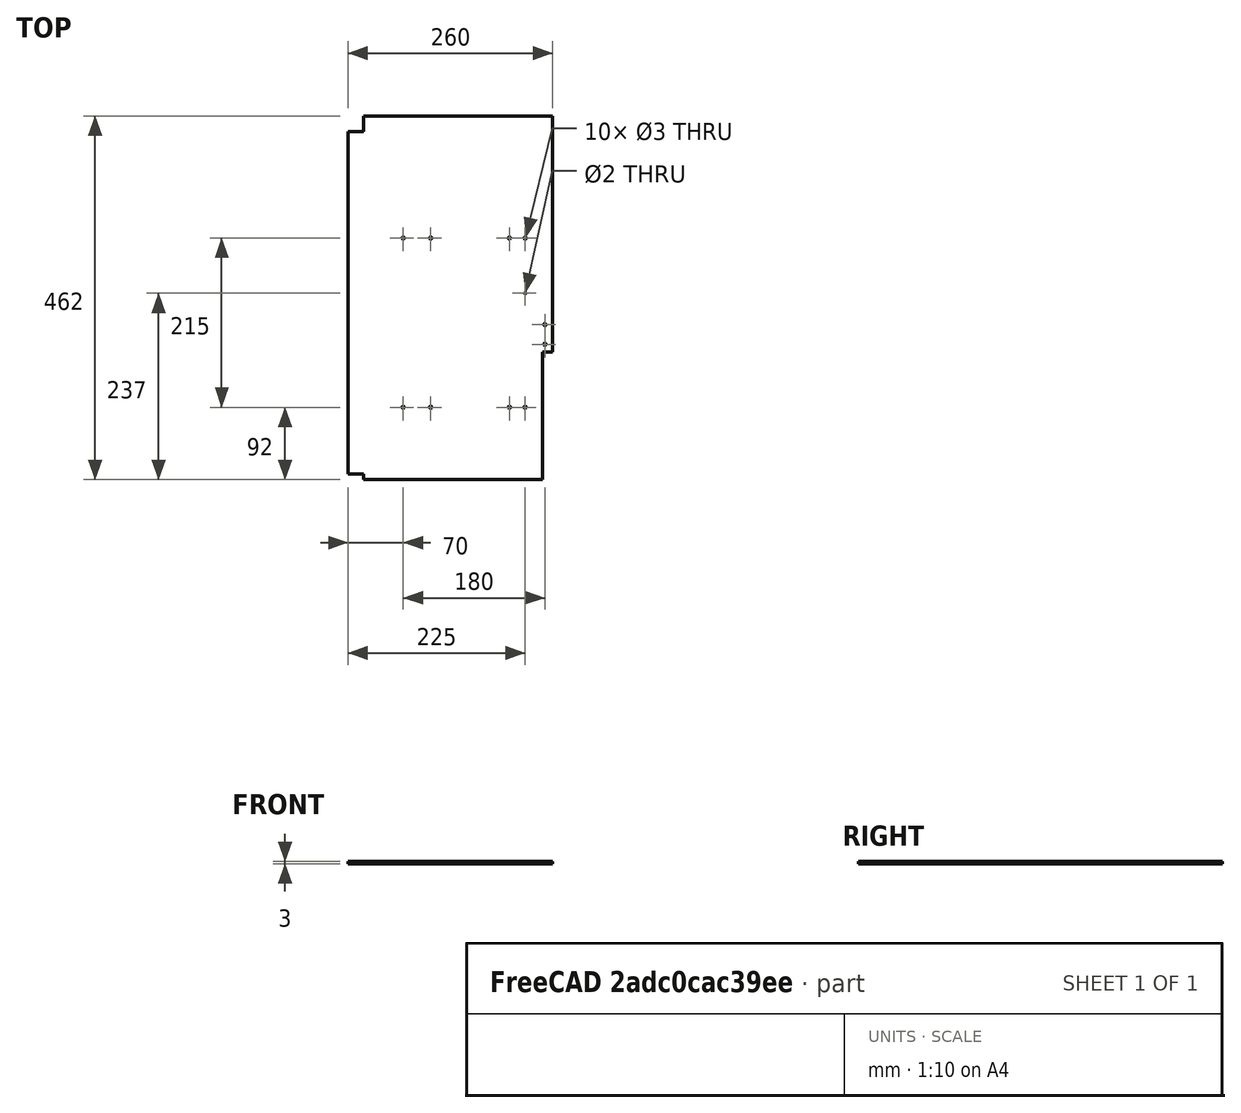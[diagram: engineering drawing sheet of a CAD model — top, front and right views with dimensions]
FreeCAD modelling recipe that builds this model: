
FCSTD DOCUMENT  (FreeCAD 0.18R)
Label: K-MINI-Enclosure-BottomChamberSheet
License: All rights reserved
LicenseURL: http://en.wikipedia.org/wiki/All_rights_reserved
objects: Drawing::FeatureViewPython×19, Sketcher::SketchObject×1, PartDesign::Pad×1, PartDesign::Body×1, App::Part×1, Drawing::FeatureViewPart×1, Drawing::FeaturePage×1
note: 4 computed .brp shape members not serialized (recipe doc carries the construction recipe); baked Part::Feature solids carry a one-line shape summary decoded from their .brp

FEATURE [Sketcher::SketchObject] Sketch020
  MapMode = 5
  Support = -> [XY_Plane042]
  sketch-geometry (21):
    g0: LineSegment StartX=-205 StartY=-237 StartZ=0 EndX=22 EndY=-237 EndZ=0
    g1: LineSegment StartX=35 StartY=225 StartZ=0 EndX=-205 EndY=225 EndZ=0
    g2: LineSegment StartX=-205 StartY=225 StartZ=0 EndX=-205 EndY=205 EndZ=0
    g3: LineSegment StartX=-205 StartY=205 StartZ=0 EndX=-225 EndY=205 EndZ=0
    g4: LineSegment StartX=-225 StartY=205 StartZ=0 EndX=-225 EndY=-230 EndZ=0
    g5: LineSegment StartX=-225 StartY=-230 StartZ=0 EndX=-205 EndY=-230 EndZ=0
    g6: LineSegment StartX=-205 StartY=-230 StartZ=0 EndX=-205 EndY=-237 EndZ=0
    g7: Circle CenterX=-155 CenterY=70 CenterZ=0 NormalX=0 NormalY=0 NormalZ=1 AngleXU=0 Radius=1.5
    g8: Circle CenterX=-120 CenterY=70 CenterZ=0 NormalX=0 NormalY=0 NormalZ=1 AngleXU=0 Radius=1.5
    g9: Circle CenterX=25 CenterY=-40 CenterZ=0 NormalX=0 NormalY=0 NormalZ=1 AngleXU=0 Radius=1.5
    g10: Circle CenterX=25 CenterY=-65 CenterZ=0 NormalX=0 NormalY=0 NormalZ=1 AngleXU=0 Radius=1.5
    g11: Circle CenterX=-120 CenterY=-145 CenterZ=0 NormalX=0 NormalY=0 NormalZ=1 AngleXU=0 Radius=1.5
    g12: Circle CenterX=-155 CenterY=-145 CenterZ=0 NormalX=0 NormalY=0 NormalZ=1 AngleXU=0 Radius=1.5
    g13: Circle CenterX=0 CenterY=0 CenterZ=0 NormalX=0 NormalY=0 NormalZ=1 AngleXU=0 Radius=1
    g14: Circle CenterX=-20 CenterY=70 CenterZ=0 NormalX=0 NormalY=0 NormalZ=1 AngleXU=0 Radius=1.5
    g15: Circle CenterX=0 CenterY=70 CenterZ=0 NormalX=0 NormalY=0 NormalZ=1 AngleXU=0 Radius=1.5
    g16: Circle CenterX=-20 CenterY=-145 CenterZ=0 NormalX=0 NormalY=0 NormalZ=1 AngleXU=0 Radius=1.5
    g17: Circle CenterX=0 CenterY=-145 CenterZ=0 NormalX=0 NormalY=0 NormalZ=1 AngleXU=0 Radius=1.5
    g18: LineSegment StartX=22 StartY=-237 StartZ=0 EndX=22 EndY=-75 EndZ=0
    g19: LineSegment StartX=22 StartY=-75 StartZ=0 EndX=35 EndY=-75 EndZ=0
    g20: LineSegment StartX=35 StartY=-75 StartZ=0 EndX=35 EndY=225 EndZ=0
  constraints (62):
    c: Coincident(g1,g2)
    c: Coincident(g2,g3)
    c: Coincident(g3,g4)
    c: Coincident(g4,g5)
    c: Coincident(g5,g6)
    c: Horizontal(g0)
    c: Horizontal(g1)
    c: Horizontal(g5)
    c: Vertical(g4)
    c: Vertical(g2)
    c: Vertical(g6)
    c: Horizontal(g3)
    c: DistanceY(g2,g2) = 20
    c: DistanceX(g3,g3) = 20
    c: DistanceX(g5,g5) = 20
    c: DistanceY(g6,g6) = 7
    c: DistanceX(g1,g-1) = 205
    c: DistanceY(g-1,g1) = 225
    c: Coincident(g0,g6)
    c: Radius(g12) = 1.5
    c: Equal(g10,g9)
    c: Equal(g9,g8)
    c: Equal(g8,g7)
    c: Equal(g7,g11)
    c: Equal(g11,g12)
    c: Horizontal(g7,g8)
    c: Vertical(g9,g10)
    c: Horizontal(g11,g12)
    c: DistanceY(g-1,g7) = 70
    c: DistanceY(g12,g-1) = 145
    c: DistanceX(g7,g8) = 35
    c: DistanceY(g10,g9) = 25
    c: DistanceY(g9,g-1) = 40
    c: DistanceX(g-1,g9) = 25
    c: Coincident(g13,g-1)
    c: Radius(g13) = 1
    c: Horizontal(g14,g15)
    c: Horizontal(g15,g8)
    c: Horizontal(g11,g16)
    c: Horizontal(g16,g17)
    c: DistanceX(g8,g15) = 120
    c: DistanceX(g14,g15) = 20
    c: Vertical(g15,g17)
    c: Vertical(g14,g16)
    c: Equal(g8,g14)
    c: Equal(g14,g15)
    c: Equal(g15,g16)
    c: Equal(g16,g17)
    c: DistanceY(g0,g13) = 237
    c: Coincident(g19,g20)
    c: Coincident(g0,g18)
    c: Coincident(g18,g19)
    c: Horizontal(g19)
    c: Vertical(g20)
    c: Vertical(g18)
    c: DistanceX(g13,g0) = 22
    c: Vertical(g11,g8)
    c: Vertical(g12,g7)
    c: DistanceY(g18,g18) = 162
    c: PointOnObject(g17,g-2)
    c: DistanceX(g3,g20) = 260
    c: Coincident(g1,g20)
FEATURE [PartDesign::Pad] Pad034
  Length = 3
  Length2 = 100
  Profile = -> Sketch020
  Type = 0
FEATURE [PartDesign::Body] Body035  label="BottomEnclosureSheet"
  Group = -> [Sketch020,Pad034]
  Origin = -> Origin042
  Placement = pos=(0,0,-30) rot=(0,0,1;0rad)
  Tip = -> Pad034
FEATURE [App::Part] Part002  label="K-MINI-Enclosure-BottomChamberSheet"
  Group = -> [Body035]
  Origin = -> Origin004
FEATURE [Drawing::FeatureViewPart] View
  Direction = (0,0,1)
  HiddenWidth = 0.15
  LineWidth = 0.35
  Rotation = 90
  ShowHiddenLines = false
  ShowSmoothLines = false
  Source = -> Body035
  Tolerance = 0.05
  ViewResult = <g id="View"\n   transform="rotate(90,300,300) translate(300,300) scale(1,1)"\n  >\n<g   fill="none"\n   stroke="rgb(0, 0, 0)"\n   stroke-linecap="butt"\n   stroke-linejoin="miter"\n   stroke-width="0.350000"\n   transform="scale(1,-1)"\n  >\n<path id= "1" d=" M -205 -237 L 22 -237 " />\n<path id= "2" d=" M 22 -237 L 22 -75 " />\n<path id= "3" d=" M 22 -75 L 35 -75 " />\n<path id= "4" d=" M 35 -75 L 35 225 " />\n<path id= "5" d=" M 35 225 L -205 225 " />\n<path id= "6" d=" M -205 225 L -205 205 " />\n<path id= "7" d=" M -205 205 L -225 205 " />\n<path id= "8" d=" M -225 205 L -225 -230 " />\n<path id= "9" d=" M -225 -230 L -205 -230 " />\n<path id= "10" d=" M -205 -230 L -205 -237 " />\n<circle cx ="0" cy ="-145" r ="1.5" /><circle cx ="-20" cy ="-145" r ="1.5" /><circle cx ="0" cy ="70" r ="1.5" /><circle cx ="-20" cy ="70" r ="1.5" /><circle cx ="-155" cy ="-145" r ="1.5" /><circle cx ="-120" cy ="-145" r ="1.5" /><circle cx ="25" cy ="-65" r ="1.5" /><circle cx ="25" cy ="-40" r ="1.5" /><circle cx ="-120" cy ="70" r ="1.5" /><circle cx ="-155" cy ="70" r ="1.5" /><circle cx ="0" cy ="0" r ="1" /></g>\n</g>
  Visible = true
  X = 300
  Y = 300
FEATURE [Drawing::FeatureViewPython] dim001  # drawing view (typed FeaturePython)
  Rotation = 0
  ViewResult = <g> \n  <line x1="68.000000" y1="75.000000" x2="30.314251" y2="75.000000" style="stroke:rgb(0,0,255);stroke-width:0.50" />\n<line x1="61.000000" y1="322.000000" x2="30.314251" y2="322.000000" style="stroke:rgb(0,0,255);stroke-width:0.50" />\n<line x1="31.314251" y1="75.000000" x2="31.314251" y2="322.000000" style="stroke:rgb(0,0,255);stroke-width:0.50" /> \n  <polygon points="31.314251,322.000000 32.314251,319.000000 31.314251,318.000000 30.314251,319.000000" style="fill:rgb(0,0,255);stroke:rgb(0,0,255);stroke-width:0" /><polygon points="31.314251,75.000000 30.314251,78.000000 31.314251,79.000000 32.314251,78.000000" style="fill:rgb(0,0,255);stroke:rgb(0,0,255);stroke-width:0" /> \n  <text x="29.314251" y="198.500000" font-family="inherit" font-size="3.6" fill="rgb(0,0,255)" text-anchor="middle" transform="rotate(-90.000000 29.314251,198.500000)" >247</text> </g>
  Visible = true
  X = 0
  Y = 0
  arrowL1 = 3
  arrowL2 = 1
  arrowW = 2
  arrow_scheme = 0
  autoPlaceOffset = 2
  autoPlaceText = true
  click1_x = 31.3143
  click1_y = 315.491
  click2_x = 31.3143
  click2_y = 315.491
  comma_decimal_place = false
  dimension_line_overshoot = 1
  gap_datum_points = 2
  halfDimension_linear = false
  lineColor = rgb(0,0,255)
  strokeWidth = 0.5
  textFormat_linear = %(value)3.3f
  textRenderer_color = rgb(0,0,255)
  textRenderer_family = inherit
  textRenderer_size = 3.6
  unit_custom_scale = 1
  unit_scheme = 0
FEATURE [Drawing::FeatureViewPython] dim002  # drawing view (typed FeaturePython)
  Rotation = 0
  ViewResult = <g> \n  <line x1="68.000000" y1="75.000000" x2="45.188520" y2="75.000000" style="stroke:rgb(0,0,255);stroke-width:0.50" />\n<line x1="68.000000" y1="95.000000" x2="45.188520" y2="95.000000" style="stroke:rgb(0,0,255);stroke-width:0.50" />\n<line x1="46.188520" y1="75.000000" x2="46.188520" y2="95.000000" style="stroke:rgb(0,0,255);stroke-width:0.50" /> \n  <polygon points="46.188520,95.000000 47.188520,92.000000 46.188520,91.000000 45.188520,92.000000" style="fill:rgb(0,0,255);stroke:rgb(0,0,255);stroke-width:0" /><polygon points="46.188520,75.000000 45.188520,78.000000 46.188520,79.000000 47.188520,78.000000" style="fill:rgb(0,0,255);stroke:rgb(0,0,255);stroke-width:0" /> \n  <text x="44.188520" y="85.000000" font-family="inherit" font-size="3.6" fill="rgb(0,0,255)" text-anchor="middle" transform="rotate(-90.000000 44.188520,85.000000)" >20</text> </g>
  Visible = true
  X = 0
  Y = 0
  arrowL1 = 3
  arrowL2 = 1
  arrowW = 2
  arrow_scheme = 0
  autoPlaceOffset = 2
  autoPlaceText = true
  click1_x = 46.1885
  click1_y = 96.6827
  click2_x = 46.1885
  click2_y = 96.6827
  comma_decimal_place = false
  dimension_line_overshoot = 1
  gap_datum_points = 2
  halfDimension_linear = false
  lineColor = rgb(0,0,255)
  strokeWidth = 0.5
  textFormat_linear = %(value)3.3f
  textRenderer_color = rgb(0,0,255)
  textRenderer_family = inherit
  textRenderer_size = 3.6
  unit_custom_scale = 1
  unit_scheme = 0
FEATURE [Drawing::FeatureViewPython] dim003  # drawing view (typed FeaturePython)
  Rotation = 0
  ViewResult = <g> \n  <line x1="63.000000" y1="93.000000" x2="63.000000" y2="60.454217" style="stroke:rgb(0,0,255);stroke-width:0.50" />\n<line x1="70.000000" y1="73.000000" x2="70.000000" y2="60.454217" style="stroke:rgb(0,0,255);stroke-width:0.50" />\n<line x1="63.000000" y1="61.454217" x2="70.000000" y2="61.454217" style="stroke:rgb(0,0,255);stroke-width:0.50" /> \n  <polygon points="70.000000,61.454217 73.000000,62.454217 74.000000,61.454217 73.000000,60.454217" style="fill:rgb(0,0,255);stroke:rgb(0,0,255);stroke-width:0" /><polygon points="63.000000,61.454217 60.000000,60.454217 59.000000,61.454217 60.000000,62.454217" style="fill:rgb(0,0,255);stroke:rgb(0,0,255);stroke-width:0" /> \n  <text x="66.500000" y="59.454217" font-family="inherit" font-size="3.6" fill="rgb(0,0,255)" text-anchor="middle" transform="rotate(0.000000 66.500000,59.454217)" >7</text> </g>
  Visible = true
  X = 0
  Y = 0
  arrowL1 = 3
  arrowL2 = 1
  arrowW = 2
  arrow_scheme = 0
  autoPlaceOffset = 2
  autoPlaceText = true
  click1_x = 64.5856
  click1_y = 61.4542
  click2_x = 64.5856
  click2_y = 61.4542
  comma_decimal_place = false
  dimension_line_overshoot = 1
  gap_datum_points = 2
  halfDimension_linear = false
  lineColor = rgb(0,0,255)
  strokeWidth = 0.5
  textFormat_linear = %(value)3.3f
  textRenderer_color = rgb(0,0,255)
  textRenderer_family = inherit
  textRenderer_size = 3.6
  unit_custom_scale = 1
  unit_scheme = 0
FEATURE [Drawing::FeatureViewPython] dim004  # drawing view (typed FeaturePython)
  Rotation = 0
  ViewResult = <g> \n  <line x1="507.000000" y1="75.000000" x2="544.693676" y2="75.000000" style="stroke:rgb(0,0,255);stroke-width:0.50" />\n<line x1="507.000000" y1="95.000000" x2="544.693676" y2="95.000000" style="stroke:rgb(0,0,255);stroke-width:0.50" />\n<line x1="543.693676" y1="75.000000" x2="543.693676" y2="95.000000" style="stroke:rgb(0,0,255);stroke-width:0.50" /> \n  <polygon points="543.693676,95.000000 544.693676,92.000000 543.693676,91.000000 542.693676,92.000000" style="fill:rgb(0,0,255);stroke:rgb(0,0,255);stroke-width:0" /><polygon points="543.693676,75.000000 542.693676,78.000000 543.693676,79.000000 544.693676,78.000000" style="fill:rgb(0,0,255);stroke:rgb(0,0,255);stroke-width:0" /> \n  <text x="541.693676" y="85.000000" font-family="inherit" font-size="3.6" fill="rgb(0,0,255)" text-anchor="middle" transform="rotate(-90.000000 541.693676,85.000000)" >20</text> </g>
  Visible = true
  X = 0
  Y = 0
  arrowL1 = 3
  arrowL2 = 1
  arrowW = 2
  arrow_scheme = 0
  autoPlaceOffset = 2
  autoPlaceText = true
  click1_x = 543.694
  click1_y = 100.988
  click2_x = 543.694
  click2_y = 100.988
  comma_decimal_place = false
  dimension_line_overshoot = 1
  gap_datum_points = 2
  halfDimension_linear = false
  lineColor = rgb(0,0,255)
  strokeWidth = 0.5
  textFormat_linear = %(value)3.3f
  textRenderer_color = rgb(0,0,255)
  textRenderer_family = inherit
  textRenderer_size = 3.6
  unit_custom_scale = 1
  unit_scheme = 0
FEATURE [Drawing::FeatureViewPython] dim005  # drawing view (typed FeaturePython)
  Rotation = 0
  ViewResult = <g> \n  <line x1="527.000000" y1="95.000000" x2="544.302248" y2="95.000000" style="stroke:rgb(0,0,255);stroke-width:0.50" />\n<line x1="527.000000" y1="322.000000" x2="544.302248" y2="322.000000" style="stroke:rgb(0,0,255);stroke-width:0.50" />\n<line x1="543.302248" y1="95.000000" x2="543.302248" y2="322.000000" style="stroke:rgb(0,0,255);stroke-width:0.50" /> \n  <polygon points="543.302248,322.000000 544.302248,319.000000 543.302248,318.000000 542.302248,319.000000" style="fill:rgb(0,0,255);stroke:rgb(0,0,255);stroke-width:0" /><polygon points="543.302248,95.000000 542.302248,98.000000 543.302248,99.000000 544.302248,98.000000" style="fill:rgb(0,0,255);stroke:rgb(0,0,255);stroke-width:0" /> \n  <text x="541.302248" y="208.500000" font-family="inherit" font-size="3.6" fill="rgb(0,0,255)" text-anchor="middle" transform="rotate(-90.000000 541.302248,208.500000)" >227</text> </g>
  Visible = true
  X = 0
  Y = 0
  arrowL1 = 3
  arrowL2 = 1
  arrowW = 2
  arrow_scheme = 0
  autoPlaceOffset = 2
  autoPlaceText = true
  click1_x = 543.302
  click1_y = 328.408
  click2_x = 543.302
  click2_y = 328.408
  comma_decimal_place = false
  dimension_line_overshoot = 1
  gap_datum_points = 2
  halfDimension_linear = false
  lineColor = rgb(0,0,255)
  strokeWidth = 0.5
  textFormat_linear = %(value)3.3f
  textRenderer_color = rgb(0,0,255)
  textRenderer_family = inherit
  textRenderer_size = 3.6
  unit_custom_scale = 1
  unit_scheme = 0
FEATURE [Drawing::FeatureViewPython] dim006  # drawing view (typed FeaturePython)
  Rotation = 0
  ViewResult = <g> \n  <line x1="507.000000" y1="75.000000" x2="560.350802" y2="75.000000" style="stroke:rgb(0,0,255);stroke-width:0.50" />\n<line x1="437.000000" y1="335.000000" x2="560.350802" y2="335.000000" style="stroke:rgb(0,0,255);stroke-width:0.50" />\n<line x1="559.350802" y1="75.000000" x2="559.350802" y2="335.000000" style="stroke:rgb(0,0,255);stroke-width:0.50" /> \n  <polygon points="559.350802,335.000000 560.350802,332.000000 559.350802,331.000000 558.350802,332.000000" style="fill:rgb(0,0,255);stroke:rgb(0,0,255);stroke-width:0" /><polygon points="559.350802,75.000000 558.350802,78.000000 559.350802,79.000000 560.350802,78.000000" style="fill:rgb(0,0,255);stroke:rgb(0,0,255);stroke-width:0" /> \n  <text x="557.350802" y="205.000000" font-family="inherit" font-size="3.6" fill="rgb(0,0,255)" text-anchor="middle" transform="rotate(-90.000000 557.350802,205.000000)" >260</text> </g>
  Visible = true
  X = 0
  Y = 0
  arrowL1 = 3
  arrowL2 = 1
  arrowW = 2
  arrow_scheme = 0
  autoPlaceOffset = 2
  autoPlaceText = true
  click1_x = 559.351
  click1_y = 315.1
  click2_x = 559.351
  click2_y = 315.1
  comma_decimal_place = false
  dimension_line_overshoot = 1
  gap_datum_points = 2
  halfDimension_linear = false
  lineColor = rgb(0,0,255)
  strokeWidth = 0.5
  textFormat_linear = %(value)3.3f
  textRenderer_color = rgb(0,0,255)
  textRenderer_family = inherit
  textRenderer_size = 3.6
  unit_custom_scale = 1
  unit_scheme = 0
FEATURE [Drawing::FeatureViewPython] dim007  # drawing view (typed FeaturePython)
  Rotation = 0
  ViewResult = <g> \n  <line x1="63.000000" y1="93.000000" x2="63.000000" y2="35.402816" style="stroke:rgb(0,0,255);stroke-width:0.50" />\n<line x1="525.000000" y1="93.000000" x2="525.000000" y2="35.402816" style="stroke:rgb(0,0,255);stroke-width:0.50" />\n<line x1="63.000000" y1="36.402816" x2="525.000000" y2="36.402816" style="stroke:rgb(0,0,255);stroke-width:0.50" /> \n  <polygon points="525.000000,36.402816 522.000000,35.402816 521.000000,36.402816 522.000000,37.402816" style="fill:rgb(0,0,255);stroke:rgb(0,0,255);stroke-width:0" /><polygon points="63.000000,36.402816 66.000000,37.402816 67.000000,36.402816 66.000000,35.402816" style="fill:rgb(0,0,255);stroke:rgb(0,0,255);stroke-width:0" /> \n  <text x="294.000000" y="34.402816" font-family="inherit" font-size="3.6" fill="rgb(0,0,255)" text-anchor="middle" transform="rotate(0.000000 294.000000,34.402816)" >462</text> </g>
  Visible = true
  X = 0
  Y = 0
  arrowL1 = 3
  arrowL2 = 1
  arrowW = 2
  arrow_scheme = 0
  autoPlaceOffset = 2
  autoPlaceText = true
  click1_x = 510.422
  click1_y = 36.4028
  click2_x = 510.422
  click2_y = 36.4028
  comma_decimal_place = false
  dimension_line_overshoot = 1
  gap_datum_points = 2
  halfDimension_linear = false
  lineColor = rgb(0,0,255)
  strokeWidth = 0.5
  textFormat_linear = %(value)3.3f
  textRenderer_color = rgb(0,0,255)
  textRenderer_family = inherit
  textRenderer_size = 3.6
  unit_custom_scale = 1
  unit_scheme = 0
FEATURE [Drawing::FeatureViewPython] dim008  # drawing view (typed FeaturePython)
  Rotation = 0
  ViewResult = <g> \n  <line x1="505.000000" y1="93.000000" x2="505.000000" y2="51.451370" style="stroke:rgb(0,0,255);stroke-width:0.50" />\n<line x1="525.000000" y1="93.000000" x2="525.000000" y2="51.451370" style="stroke:rgb(0,0,255);stroke-width:0.50" />\n<line x1="505.000000" y1="52.451370" x2="525.000000" y2="52.451370" style="stroke:rgb(0,0,255);stroke-width:0.50" /> \n  <polygon points="525.000000,52.451370 522.000000,51.451370 521.000000,52.451370 522.000000,53.451370" style="fill:rgb(0,0,255);stroke:rgb(0,0,255);stroke-width:0" /><polygon points="505.000000,52.451370 508.000000,53.451370 509.000000,52.451370 508.000000,51.451370" style="fill:rgb(0,0,255);stroke:rgb(0,0,255);stroke-width:0" /> \n  <text x="515.000000" y="50.451370" font-family="inherit" font-size="3.6" fill="rgb(0,0,255)" text-anchor="middle" transform="rotate(0.000000 515.000000,50.451370)" >20</text> </g>
  Visible = true
  X = 0
  Y = 0
  arrowL1 = 3
  arrowL2 = 1
  arrowW = 2
  arrow_scheme = 0
  autoPlaceOffset = 2
  autoPlaceText = true
  click1_x = 514.728
  click1_y = 52.4514
  click2_x = 514.728
  click2_y = 52.4514
  comma_decimal_place = false
  dimension_line_overshoot = 1
  gap_datum_points = 2
  halfDimension_linear = false
  lineColor = rgb(0,0,255)
  strokeWidth = 0.5
  textFormat_linear = %(value)3.3f
  textRenderer_color = rgb(0,0,255)
  textRenderer_family = inherit
  textRenderer_size = 3.6
  unit_custom_scale = 1
  unit_scheme = 0
FEATURE [Drawing::FeatureViewPython] dim009  # drawing view (typed FeaturePython)
  Rotation = 0
  ViewResult = <g> \n  <line x1="63.000000" y1="324.000000" x2="63.000000" y2="383.816714" style="stroke:rgb(0,0,255);stroke-width:0.50" />\n<line x1="225.000000" y1="324.000000" x2="225.000000" y2="383.816714" style="stroke:rgb(0,0,255);stroke-width:0.50" />\n<line x1="63.000000" y1="382.816714" x2="225.000000" y2="382.816714" style="stroke:rgb(0,0,255);stroke-width:0.50" /> \n  <polygon points="225.000000,382.816714 222.000000,381.816714 221.000000,382.816714 222.000000,383.816714" style="fill:rgb(0,0,255);stroke:rgb(0,0,255);stroke-width:0" /><polygon points="63.000000,382.816714 66.000000,383.816714 67.000000,382.816714 66.000000,381.816714" style="fill:rgb(0,0,255);stroke:rgb(0,0,255);stroke-width:0" /> \n  <text x="144.000000" y="380.816714" font-family="inherit" font-size="3.6" fill="rgb(0,0,255)" text-anchor="middle" transform="rotate(0.000000 144.000000,380.816714)" >162</text> </g>
  Visible = true
  X = 0
  Y = 0
  arrowL1 = 3
  arrowL2 = 1
  arrowW = 2
  arrow_scheme = 0
  autoPlaceOffset = 2
  autoPlaceText = true
  click1_x = 227.42
  click1_y = 382.817
  click2_x = 227.42
  click2_y = 382.817
  comma_decimal_place = false
  dimension_line_overshoot = 1
  gap_datum_points = 2
  halfDimension_linear = false
  lineColor = rgb(0,0,255)
  strokeWidth = 0.5
  textFormat_linear = %(value)3.3f
  textRenderer_color = rgb(0,0,255)
  textRenderer_family = inherit
  textRenderer_size = 3.6
  unit_custom_scale = 1
  unit_scheme = 0
FEATURE [Drawing::FeatureViewPython] dim011  # drawing view (typed FeaturePython)
  Rotation = 0
  ViewResult = <g> \n  <line x1="368.000000" y1="180.000000" x2="315.035421" y2="180.000000" style="stroke:rgb(0,0,255);stroke-width:0.50" />\n<line x1="503.000000" y1="75.000000" x2="315.035421" y2="75.000000" style="stroke:rgb(0,0,255);stroke-width:0.50" />\n<line x1="316.035421" y1="180.000000" x2="316.035421" y2="75.000000" style="stroke:rgb(0,0,255);stroke-width:0.50" /> \n  <polygon points="316.035421,75.000000 315.035421,78.000000 316.035421,79.000000 317.035421,78.000000" style="fill:rgb(0,0,255);stroke:rgb(0,0,255);stroke-width:0" /><polygon points="316.035421,180.000000 317.035421,177.000000 316.035421,176.000000 315.035421,177.000000" style="fill:rgb(0,0,255);stroke:rgb(0,0,255);stroke-width:0" /> \n  <text x="314.035421" y="127.500000" font-family="inherit" font-size="3.6" fill="rgb(0,0,255)" text-anchor="middle" transform="rotate(-90.000000 314.035421,127.500000)" >105</text> </g>
  Visible = true
  X = 0
  Y = 0
  arrowL1 = 3
  arrowL2 = 1
  arrowW = 2
  arrow_scheme = 0
  autoPlaceOffset = 2
  autoPlaceText = true
  click1_x = 316.035
  click1_y = 94.2592
  click2_x = 316.035
  click2_y = 94.2592
  comma_decimal_place = false
  dimension_line_overshoot = 1
  gap_datum_points = 2
  halfDimension_linear = false
  lineColor = rgb(0,0,255)
  strokeWidth = 0.5
  textFormat_linear = %(value)3.3f
  textRenderer_color = rgb(0,0,255)
  textRenderer_family = inherit
  textRenderer_size = 3.6
  unit_custom_scale = 1
  unit_scheme = 0
FEATURE [Drawing::FeatureViewPython] dim012  # drawing view (typed FeaturePython)
  Rotation = 0
  ViewResult = <g> \n  <line x1="368.000000" y1="180.000000" x2="347.945273" y2="180.000000" style="stroke:rgb(0,0,255);stroke-width:0.50" />\n<line x1="368.000000" y1="145.000000" x2="347.945273" y2="145.000000" style="stroke:rgb(0,0,255);stroke-width:0.50" />\n<line x1="348.945273" y1="180.000000" x2="348.945273" y2="145.000000" style="stroke:rgb(0,0,255);stroke-width:0.50" /> \n  <polygon points="348.945273,145.000000 347.945273,148.000000 348.945273,149.000000 349.945273,148.000000" style="fill:rgb(0,0,255);stroke:rgb(0,0,255);stroke-width:0" /><polygon points="348.945273,180.000000 349.945273,177.000000 348.945273,176.000000 347.945273,177.000000" style="fill:rgb(0,0,255);stroke:rgb(0,0,255);stroke-width:0" /> \n  <text x="346.945273" y="162.500000" font-family="inherit" font-size="3.6" fill="rgb(0,0,255)" text-anchor="middle" transform="rotate(-90.000000 346.945273,162.500000)" >35</text> </g>
  Visible = true
  X = 0
  Y = 0
  arrowL1 = 3
  arrowL2 = 1
  arrowW = 2
  arrow_scheme = 0
  autoPlaceOffset = 2
  autoPlaceText = true
  click1_x = 348.945
  click1_y = 145.345
  click2_x = 348.945
  click2_y = 145.345
  comma_decimal_place = false
  dimension_line_overshoot = 1
  gap_datum_points = 2
  halfDimension_linear = false
  lineColor = rgb(0,0,255)
  strokeWidth = 0.5
  textFormat_linear = %(value)3.3f
  textRenderer_color = rgb(0,0,255)
  textRenderer_family = inherit
  textRenderer_size = 3.6
  unit_custom_scale = 1
  unit_scheme = 0
FEATURE [Drawing::FeatureViewPython] dim013  # drawing view (typed FeaturePython)
  Rotation = 0
  ViewResult = <g> \n  <line x1="258.000000" y1="325.000000" x2="228.562723" y2="325.000000" style="stroke:rgb(0,0,255);stroke-width:0.50" />\n<line x1="298.000000" y1="300.000000" x2="228.562723" y2="300.000000" style="stroke:rgb(0,0,255);stroke-width:0.50" />\n<line x1="229.562723" y1="325.000000" x2="229.562723" y2="300.000000" style="stroke:rgb(0,0,255);stroke-width:0.50" /> \n  <polygon points="229.562723,300.000000 228.562723,303.000000 229.562723,304.000000 230.562723,303.000000" style="fill:rgb(0,0,255);stroke:rgb(0,0,255);stroke-width:0" /><polygon points="229.562723,325.000000 230.562723,322.000000 229.562723,321.000000 228.562723,322.000000" style="fill:rgb(0,0,255);stroke:rgb(0,0,255);stroke-width:0" /> \n  <text x="227.562723" y="312.500000" font-family="inherit" font-size="3.6" fill="rgb(0,0,255)" text-anchor="middle" transform="rotate(-90.000000 227.562723,312.500000)" >25</text> </g>
  Visible = true
  X = 0
  Y = 0
  arrowL1 = 3
  arrowL2 = 1
  arrowW = 2
  arrow_scheme = 0
  autoPlaceOffset = 2
  autoPlaceText = true
  click1_x = 229.563
  click1_y = 315.952
  click2_x = 229.563
  click2_y = 315.952
  comma_decimal_place = false
  dimension_line_overshoot = 1
  gap_datum_points = 2
  halfDimension_linear = false
  lineColor = rgb(0,0,255)
  strokeWidth = 0.5
  textFormat_linear = %(value)3.3f
  textRenderer_color = rgb(0,0,255)
  textRenderer_family = inherit
  textRenderer_size = 3.6
  unit_custom_scale = 1
  unit_scheme = 0
FEATURE [Drawing::FeatureViewPython] dim014  # drawing view (typed FeaturePython)
  Rotation = 0
  ViewResult = <g> \n  <line x1="368.000000" y1="180.000000" x2="111.052618" y2="180.000000" style="stroke:rgb(0,0,255);stroke-width:0.50" />\n<line x1="368.000000" y1="300.000000" x2="111.052618" y2="300.000000" style="stroke:rgb(0,0,255);stroke-width:0.50" />\n<line x1="112.052618" y1="180.000000" x2="112.052618" y2="300.000000" style="stroke:rgb(0,0,255);stroke-width:0.50" /> \n  <polygon points="112.052618,300.000000 113.052618,297.000000 112.052618,296.000000 111.052618,297.000000" style="fill:rgb(0,0,255);stroke:rgb(0,0,255);stroke-width:0" /><polygon points="112.052618,180.000000 111.052618,183.000000 112.052618,184.000000 113.052618,183.000000" style="fill:rgb(0,0,255);stroke:rgb(0,0,255);stroke-width:0" /> \n  <text x="110.052618" y="240.000000" font-family="inherit" font-size="3.6" fill="rgb(0,0,255)" text-anchor="middle" transform="rotate(-90.000000 110.052618,240.000000)" >120</text> </g>
  Visible = true
  X = 0
  Y = 0
  arrowL1 = 3
  arrowL2 = 1
  arrowW = 2
  arrow_scheme = 0
  autoPlaceOffset = 2
  autoPlaceText = true
  click1_x = 112.053
  click1_y = 291.601
  click2_x = 112.053
  click2_y = 291.601
  comma_decimal_place = false
  dimension_line_overshoot = 1
  gap_datum_points = 2
  halfDimension_linear = false
  lineColor = rgb(0,0,255)
  strokeWidth = 0.5
  textFormat_linear = %(value)3.3f
  textRenderer_color = rgb(0,0,255)
  textRenderer_family = inherit
  textRenderer_size = 3.6
  unit_custom_scale = 1
  unit_scheme = 0
FEATURE [Drawing::FeatureViewPython] dim015  # drawing view (typed FeaturePython)
  Rotation = 0
  ViewResult = <g> \n  <line x1="368.000000" y1="300.000000" x2="133.992524" y2="300.000000" style="stroke:rgb(0,0,255);stroke-width:0.50" />\n<line x1="368.000000" y1="280.000000" x2="133.992524" y2="280.000000" style="stroke:rgb(0,0,255);stroke-width:0.50" />\n<line x1="134.992524" y1="300.000000" x2="134.992524" y2="280.000000" style="stroke:rgb(0,0,255);stroke-width:0.50" /> \n  <polygon points="134.992524,280.000000 133.992524,283.000000 134.992524,284.000000 135.992524,283.000000" style="fill:rgb(0,0,255);stroke:rgb(0,0,255);stroke-width:0" /><polygon points="134.992524,300.000000 135.992524,297.000000 134.992524,296.000000 133.992524,297.000000" style="fill:rgb(0,0,255);stroke:rgb(0,0,255);stroke-width:0" /> \n  <text x="132.992524" y="290.000000" font-family="inherit" font-size="3.6" fill="rgb(0,0,255)" text-anchor="middle" transform="rotate(-90.000000 132.992524,290.000000)" >20</text> </g>
  Visible = true
  X = 0
  Y = 0
  arrowL1 = 3
  arrowL2 = 1
  arrowW = 2
  arrow_scheme = 0
  autoPlaceOffset = 2
  autoPlaceText = true
  click1_x = 134.993
  click1_y = 278.588
  click2_x = 134.993
  click2_y = 278.588
  comma_decimal_place = false
  dimension_line_overshoot = 1
  gap_datum_points = 2
  halfDimension_linear = false
  lineColor = rgb(0,0,255)
  strokeWidth = 0.5
  textFormat_linear = %(value)3.3f
  textRenderer_color = rgb(0,0,255)
  textRenderer_family = inherit
  textRenderer_size = 3.6
  unit_custom_scale = 1
  unit_scheme = 0
FEATURE [Drawing::FeatureViewPython] dim016  # drawing view (typed FeaturePython)
  Rotation = 0
  ViewResult = <g> \n  <line x1="260.000000" y1="323.000000" x2="260.000000" y2="310.807223" style="stroke:rgb(0,0,255);stroke-width:0.50" />\n<line x1="370.000000" y1="302.000000" x2="370.000000" y2="312.807223" style="stroke:rgb(0,0,255);stroke-width:0.50" />\n<line x1="260.000000" y1="311.807223" x2="370.000000" y2="311.807223" style="stroke:rgb(0,0,255);stroke-width:0.50" /> \n  <polygon points="370.000000,311.807223 367.000000,310.807223 366.000000,311.807223 367.000000,312.807223" style="fill:rgb(0,0,255);stroke:rgb(0,0,255);stroke-width:0" /><polygon points="260.000000,311.807223 263.000000,312.807223 264.000000,311.807223 263.000000,310.807223" style="fill:rgb(0,0,255);stroke:rgb(0,0,255);stroke-width:0" /> \n  <text x="315.000000" y="309.807223" font-family="inherit" font-size="3.6" fill="rgb(0,0,255)" text-anchor="middle" transform="rotate(0.000000 315.000000,309.807223)" >110</text> </g>
  Visible = true
  X = 0
  Y = 0
  arrowL1 = 3
  arrowL2 = 1
  arrowW = 2
  arrow_scheme = 0
  autoPlaceOffset = 2
  autoPlaceText = true
  click1_x = 364.108
  click1_y = 311.807
  click2_x = 364.108
  click2_y = 311.807
  comma_decimal_place = false
  dimension_line_overshoot = 1
  gap_datum_points = 2
  halfDimension_linear = false
  lineColor = rgb(0,0,255)
  strokeWidth = 0.5
  textFormat_linear = %(value)3.3f
  textRenderer_color = rgb(0,0,255)
  textRenderer_family = inherit
  textRenderer_size = 3.6
  unit_custom_scale = 1
  unit_scheme = 0
FEATURE [Drawing::FeatureViewPython] dim017  # drawing view (typed FeaturePython)
  Rotation = 0
  ViewResult = <g> \n  <line x1="370.000000" y1="298.000000" x2="370.000000" y2="288.120783" style="stroke:rgb(0,0,255);stroke-width:0.50" />\n<line x1="300.000000" y1="298.000000" x2="300.000000" y2="288.120783" style="stroke:rgb(0,0,255);stroke-width:0.50" />\n<line x1="370.000000" y1="289.120783" x2="300.000000" y2="289.120783" style="stroke:rgb(0,0,255);stroke-width:0.50" /> \n  <polygon points="300.000000,289.120783 303.000000,290.120783 304.000000,289.120783 303.000000,288.120783" style="fill:rgb(0,0,255);stroke:rgb(0,0,255);stroke-width:0" /><polygon points="370.000000,289.120783 367.000000,288.120783 366.000000,289.120783 367.000000,290.120783" style="fill:rgb(0,0,255);stroke:rgb(0,0,255);stroke-width:0" /> \n  <text x="335.000000" y="287.120783" font-family="inherit" font-size="3.6" fill="rgb(0,0,255)" text-anchor="middle" transform="rotate(-0.000000 335.000000,287.120783)" >70</text> </g>
  Visible = true
  X = 0
  Y = 0
  arrowL1 = 3
  arrowL2 = 1
  arrowW = 2
  arrow_scheme = 0
  autoPlaceOffset = 2
  autoPlaceText = true
  click1_x = 299.278
  click1_y = 289.121
  click2_x = 299.278
  click2_y = 289.121
  comma_decimal_place = false
  dimension_line_overshoot = 1
  gap_datum_points = 2
  halfDimension_linear = false
  lineColor = rgb(0,0,255)
  strokeWidth = 0.5
  textFormat_linear = %(value)3.3f
  textRenderer_color = rgb(0,0,255)
  textRenderer_family = inherit
  textRenderer_size = 3.6
  unit_custom_scale = 1
  unit_scheme = 0
FEATURE [Drawing::FeatureViewPython] dim018  # drawing view (typed FeaturePython)
  Rotation = 0
  ViewResult = <g> \n  <line x1="370.000000" y1="298.000000" x2="370.000000" y2="44.522889" style="stroke:rgb(0,0,255);stroke-width:0.50" />\n<line x1="525.000000" y1="93.000000" x2="525.000000" y2="44.522889" style="stroke:rgb(0,0,255);stroke-width:0.50" />\n<line x1="370.000000" y1="45.522889" x2="525.000000" y2="45.522889" style="stroke:rgb(0,0,255);stroke-width:0.50" /> \n  <polygon points="525.000000,45.522889 522.000000,44.522889 521.000000,45.522889 522.000000,46.522889" style="fill:rgb(0,0,255);stroke:rgb(0,0,255);stroke-width:0" /><polygon points="370.000000,45.522889 373.000000,46.522889 374.000000,45.522889 373.000000,44.522889" style="fill:rgb(0,0,255);stroke:rgb(0,0,255);stroke-width:0" /> \n  <text x="447.500000" y="43.522889" font-family="inherit" font-size="3.6" fill="rgb(0,0,255)" text-anchor="middle" transform="rotate(0.000000 447.500000,43.522889)" >155</text> </g>
  Visible = true
  X = 0
  Y = 0
  arrowL1 = 3
  arrowL2 = 1
  arrowW = 2
  arrow_scheme = 0
  autoPlaceOffset = 2
  autoPlaceText = true
  click1_x = 458.418
  click1_y = 45.5229
  click2_x = 458.418
  click2_y = 45.5229
  comma_decimal_place = false
  dimension_line_overshoot = 1
  gap_datum_points = 2
  halfDimension_linear = false
  lineColor = rgb(0,0,255)
  strokeWidth = 0.5
  textFormat_linear = %(value)3.3f
  textRenderer_color = rgb(0,0,255)
  textRenderer_family = inherit
  textRenderer_size = 3.6
  unit_custom_scale = 1
  unit_scheme = 0
FEATURE [Drawing::FeatureViewPython] dim019  # drawing view (typed FeaturePython)
  Rotation = 0
  ViewResult = <g> \n  <line x1="260.000000" y1="323.000000" x2="260.000000" y2="310.473176" style="stroke:rgb(0,0,255);stroke-width:0.50" />\n<line x1="235.000000" y1="323.000000" x2="235.000000" y2="310.473176" style="stroke:rgb(0,0,255);stroke-width:0.50" />\n<line x1="260.000000" y1="311.473176" x2="235.000000" y2="311.473176" style="stroke:rgb(0,0,255);stroke-width:0.50" /> \n  <polygon points="235.000000,311.473176 238.000000,312.473176 239.000000,311.473176 238.000000,310.473176" style="fill:rgb(0,0,255);stroke:rgb(0,0,255);stroke-width:0" /><polygon points="260.000000,311.473176 257.000000,310.473176 256.000000,311.473176 257.000000,312.473176" style="fill:rgb(0,0,255);stroke:rgb(0,0,255);stroke-width:0" /> \n  <text x="247.500000" y="309.473176" font-family="inherit" font-size="3.6" fill="rgb(0,0,255)" text-anchor="middle" transform="rotate(0.000000 247.500000,309.473176)" >25</text> </g>
  Visible = true
  X = 0
  Y = 0
  arrowL1 = 3
  arrowL2 = 1
  arrowW = 2
  arrow_scheme = 0
  autoPlaceOffset = 2
  autoPlaceText = true
  click1_x = 236.59
  click1_y = 311.473
  click2_x = 236.59
  click2_y = 311.473
  comma_decimal_place = false
  dimension_line_overshoot = 1
  gap_datum_points = 2
  halfDimension_linear = false
  lineColor = rgb(0,0,255)
  strokeWidth = 0.5
  textFormat_linear = %(value)3.3f
  textRenderer_color = rgb(0,0,255)
  textRenderer_family = inherit
  textRenderer_size = 3.6
  unit_custom_scale = 1
  unit_scheme = 0
FEATURE [Drawing::FeatureViewPython] dim020  # drawing view (typed FeaturePython)
  Rotation = 0
  ViewResult = <g> \n  <line x1="370.000000" y1="278.000000" x2="370.000000" y2="242.150622" style="stroke:rgb(0,0,255);stroke-width:0.50" />\n<line x1="155.000000" y1="278.000000" x2="155.000000" y2="242.150622" style="stroke:rgb(0,0,255);stroke-width:0.50" />\n<line x1="370.000000" y1="243.150622" x2="155.000000" y2="243.150622" style="stroke:rgb(0,0,255);stroke-width:0.50" /> \n  <polygon points="155.000000,243.150622 158.000000,244.150622 159.000000,243.150622 158.000000,242.150622" style="fill:rgb(0,0,255);stroke:rgb(0,0,255);stroke-width:0" /><polygon points="370.000000,243.150622 367.000000,242.150622 366.000000,243.150622 367.000000,244.150622" style="fill:rgb(0,0,255);stroke:rgb(0,0,255);stroke-width:0" /> \n  <text x="262.500000" y="241.150622" font-family="inherit" font-size="3.6" fill="rgb(0,0,255)" text-anchor="middle" transform="rotate(0.000000 262.500000,241.150622)" >215</text> </g>
  Visible = true
  X = 0
  Y = 0
  arrowL1 = 3
  arrowL2 = 1
  arrowW = 2
  arrow_scheme = 0
  autoPlaceOffset = 2
  autoPlaceText = true
  click1_x = 161.729
  click1_y = 243.151
  click2_x = 161.729
  click2_y = 243.151
  comma_decimal_place = false
  dimension_line_overshoot = 1
  gap_datum_points = 2
  halfDimension_linear = false
  lineColor = rgb(0,0,255)
  strokeWidth = 0.5
  textFormat_linear = %(value)3.3f
  textRenderer_color = rgb(0,0,255)
  textRenderer_family = inherit
  textRenderer_size = 3.6
  unit_custom_scale = 1
  unit_scheme = 0
FEATURE [Drawing::FeaturePage] Page
  Group = -> [View,dim001,dim002,dim003,dim004,dim005,dim006,dim007,dim008,dim009,dim011,dim012,dim013,dim014,dim015,dim016,dim017,dim018,dim019,dim020]
  Template = <path>
note: 1 file-system path scrubbed to <path> (originals preserved in the JSON sidecar)
